# Revit family: Electronics_Community_Biamp_Two-Way-Horn-Loaded-Full-Range-Loudspeaker_R1-EN
name_source: partatom
category: Communication Devices
units: mm (PartAtom-declared; Revit-internal decimal feet)

## family parameters
Cut with Voids When Loaded = No
Host = Face
Maintain Annotation Orientation = No
OmniClass Number = 23.85.10.11.14.14.14
OmniClass Title = Loudspeakers
Part Type = Normal
Room Calculation Point = No
Round Connector Dimension = Use Diameter
Shared = No

## types (3) — shared parameters
Connector Description = Terminal strip; 200W continuous, 800W program 40 volts RMS, 89 volts momentary peak
Crossover Frequency = 1.2 kHz
Default Elevation = 48 "
Depth = 29.76 "
Description = R1-64Z-EN Two-Way, Horn-Loaded, Type B, Full-Range Loudspeaker (60° X 40° Coverage)
Driver Protection = DYNA-TECH protection circuitry
Drivers = LF 1 x 12” weather-treated, Ferrofluid-cooled HF 1 x 1” exit, titanium diaphragm
Enclosure = Hand-laminated fiberglass, light grey gelcoat
Environmental Performance = IEC529 IP55W rating with a minimum 5-degree downward aiming angle
Grill Material = Biamp - Plastic - Gray(Grid)
Grille = 3-layer WeatherStop™, light grey (Zinc-rich epoxy dual-layer powder coated perforated steel grille, foam, woven poly mesh)
Height = 24.76 "
Housing Material = Biamp - Plastic - Gray
Input Connection = 12 foot (4 m) SJOW #16 gauge
Loudspeaker Type = 2-way horn loaded coaxial, weather-resistant
Manufacturer = Biamp
Max value position = 3
Mounting/Rigging Provisions = (5) 1/2-13 rigging points
Nominal Impedance = 6 ohms (to satisfy EN54-24 criteria)
Operating Range = 100 Hz to 10 kHz
Optional Accessories = No optional accessories are available with products intended for EN54-24 installations
Product Documentation Link = https://downloads.biamp.com
Product Page URL = https://www.biamp.com
Product data url = https://bimobject.com
Rated Noise Power = 100W continuous, 24.5 volts RMS (EN54-24 100 hr. test,6dB crest factor)
Shipping Weight = 75.00 lb
Supplied Accessories = Weather-resistant mounting yoke, light grey
URL = https://www.biamp.com
Version = 1
Weight = 55.56 lb
Width = 24.76 "
Yoke Material = Biamp - Metal - Gray

## per-type parameters (varying)
| type | Broadband Sensitivity (1W/1m) | Broadband Sensitivity (1W/4m) | Maximum Average Output (1m) | Maximum Average Output (4m) | Maximum Peak Output (1m) | Minimum Impedance | Required Accessories |
| R1-64Z-EN | 100.3 dB SPL (100Hz to 10 kHz 1/3 octave bands,EN54-24 frequency response requirements applied,EN54-24 impedance) | 88.3 dB SPL (100Hz to 10 kHz 1/3 octave bands,EN54-24 frequency response requirements applied,EN54-24 impedance) | 120.3 dB (EN54-24 frequency response requirements,100 hr. rated noise power applied, EN54-24 Broadband Sensitivity) | 108.3 dB (EN54-24 frequency response requirements,100 hr. rated noise power applied, EN54-24 Broadband Sensitivity) | 126.3 dB (EN54-24 frequency response requirements,100 hr. rated noise power applied, EN54-24 Broadband Sensitivity, 6dB crest factor momentary peak) | 5.0 ohms @ 220 Hz | 90 Hz high pass filter*, Equalization curve as specified on this spec sheet |
| R1-66Z-EN | 100.1 dB SPL (100Hz to 10 kHz 1/3 octave bands,EN54-24 frequency response requirements applied,EN54-24 impedance) | 88.1 dB SPL (100Hz to 10 kHz 1/3 octave bands,EN54-24 frequency response requirements applied,EN54-24 impedance) | 120.1 dB (EN54-24 frequency response requirements,100 hr. rated noise power applied, EN54-24 Broadband Sensitivity) | 108 dB (EN54-24 frequency response requirements,100 hr. rated noise power applied, EN54-24 Broadband Sensitivity) | 126.1 dB (EN54-24 frequency response requirements,100 hr. rated noise power applied, EN54-24 Broadband Sensitivity, 6dB crest factor momentary peak) | 5.3 ohms @ 240 Hz | 90 Hz high pass filter |
| R1-94Z-EN | 100.0 dB SPL (100Hz to 10 kHz 1/3 octave bands,EN54-24 frequency response requirements applied,EN54-24 impedance) | 87.9 dB SPL (100Hz to 10 kHz 1/3 octave bands,EN54-24 frequency response requirements applied,EN54-24 impedance) | 120.0 dB (EN54-24 frequency response requirements,100 hr. rated noise power applied, EN54-24 Broadband Sensitivity) | 107.9 dB (EN54-24 frequency response requirements,100 hr. rated noise power applied, EN54-24 Broadband Sensitivity) | 126.0 dB (EN54-24 frequency response requirements,100 hr. rated noise power applied, EN54-24 Broadband Sensitivity, 6dB crest factor momentary peak) | 5.2 ohms @ 240 Hz | 90 Hz high pass filter*, Equalization curve as specified on this spec sheet |

note: column(s) folded — value = type name in every type: Model

## geometry (parser evidence)
native form markers: Sweep x2
no freeform markers — native parametric forms only
